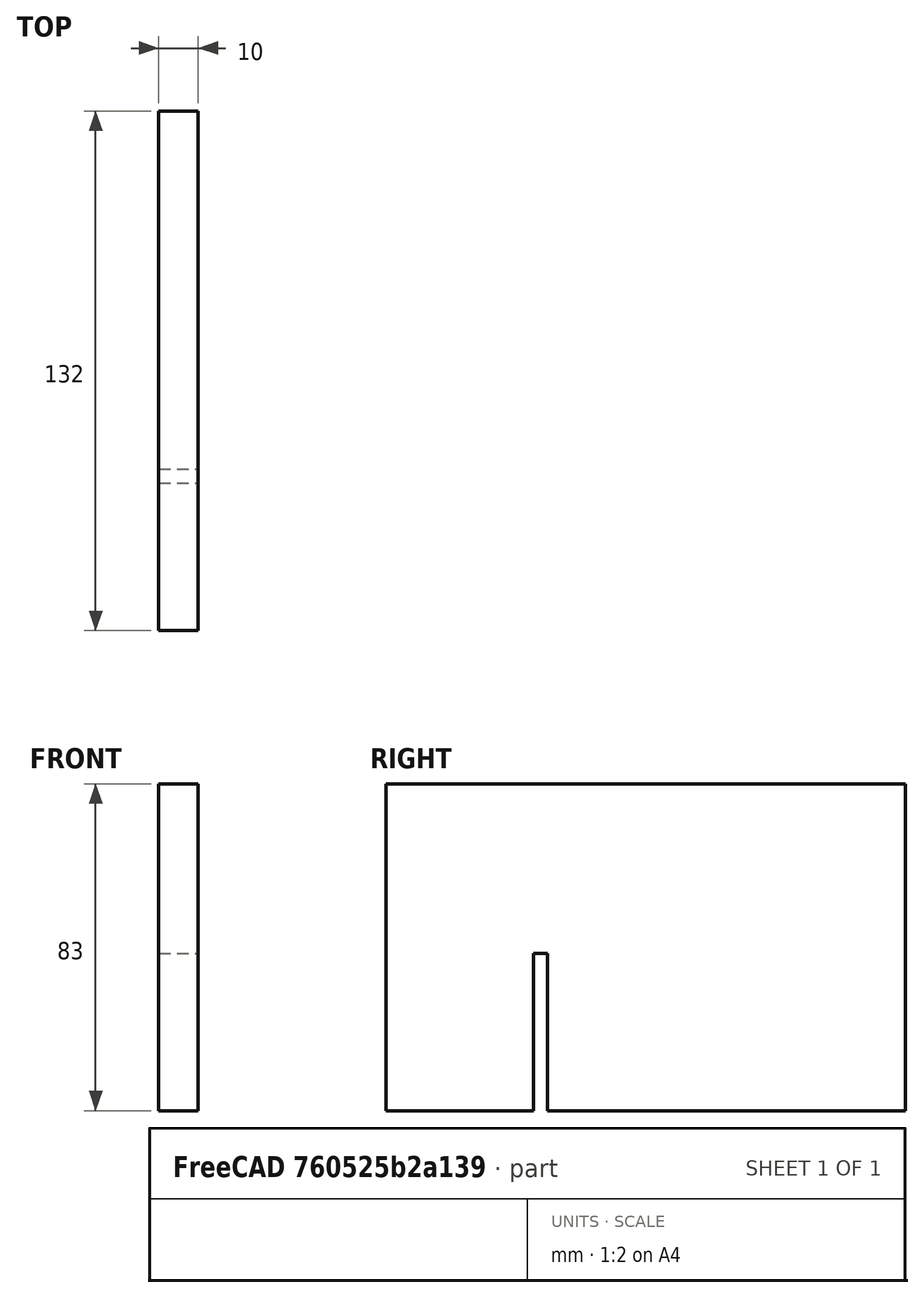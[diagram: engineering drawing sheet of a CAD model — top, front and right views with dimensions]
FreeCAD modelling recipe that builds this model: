
FCSTD DOCUMENT  (FreeCAD 0.15R4669 (Git))
Label: BR_supportMoteurN
License: All rights reserved
LicenseURL: http://en.wikipedia.org/wiki/All_rights_reserved
objects: Sketcher::SketchObject×1, Part::Extrusion×1
note: 2 computed .brp shape members not serialized (recipe doc carries the construction recipe); baked Part::Feature solids carry a one-line shape summary decoded from their .brp

FEATURE [Sketcher::SketchObject] Sketch  label="sketchSupportMoteurN"
  Placement = pos=(0,0,0) rot=(0.57735,0.57735,0.57735;2.0944rad)
  sketch-geometry (8):
    g0: LineSegment StartX=-132 StartY=-18 StartZ=0 EndX=-132 EndY=65 EndZ=0
    g1: LineSegment StartX=-132 StartY=65 StartZ=0 EndX=0 EndY=65 EndZ=0
    g2: LineSegment StartX=0 StartY=65 StartZ=0 EndX=0 EndY=-18 EndZ=0
    g3: LineSegment StartX=-132 StartY=-18 StartZ=0 EndX=-94.5 EndY=-18 EndZ=0
    g4: LineSegment StartX=-94.5 StartY=-18 StartZ=0 EndX=-94.5 EndY=22 EndZ=0
    g5: LineSegment StartX=-94.5 StartY=22 StartZ=0 EndX=-91 EndY=22 EndZ=0
    g6: LineSegment StartX=-91 StartY=22 StartZ=0 EndX=-91 EndY=-18 EndZ=0
    g7: LineSegment StartX=-91 StartY=-18 StartZ=0 EndX=0 EndY=-18 EndZ=0
  constraints (24):
    c: Coincident(g0,g1)
    c: Coincident(g1,g2)
    c: Horizontal(g1)
    c: Vertical(g0)
    c: Vertical(g2)
    c: DistanceY(g-1,g0) = 65
    c: DistanceY(g-1,g0) = -18
    c: PointOnObject(g2,g-2)
    c: Coincident(g0,g3)
    c: Horizontal(g3)
    c: Coincident(g3,g4)
    c: Vertical(g4)
    c: Coincident(g4,g5)
    c: Horizontal(g5)
    c: Coincident(g5,g6)
    c: Vertical(g6)
    c: Coincident(g6,g7)
    c: Coincident(g7,g2)
    c: Horizontal(g7)
    c: DistanceX(g1) = 132
    c: DistanceX(g6,g2) = 91
    c: DistanceX(g5) = 3.5
    c: PointOnObject(g6,g3)
    c: DistanceY(g6) = -40
FEATURE [Part::Extrusion] Extrude  label="supportMoteurN"
  Base = -> Sketch
  Dir = (10,0,0)
  Solid = true
